# Revit family: STH21910BR_30_40_STH21910PTO_30
name_source: partatom
category: Luminárias
units: mm (PartAtom-declared; Revit-internal decimal feet)

## family parameters
Compartilhado = Não
Corte com vazios quando carregada = Não
Cota do conector redondo = Utilizar diâmetro
Fonte luminosa = Sim
Hospedeiro = Forro
Manter orientação da anotação = Não
Número OmniClass = 23.80.70.11
Ponto de cálculo do ambiente = Não
Sempre na vertical = Sim
Tipo de parte = Normal
Título OmniClass = Luminaries for Internal Lighting

## types (3) — shared parameters
Altura = 0.054 m
Comprimento = 0.075 m
Cromado = Cromado
Dimerização = Não dimerizável
Fabricante = Stella
Filtro de cor = 16777215
Grau de proteção (IP) = IP20
IRC (Índice de reprodução de cores) = >80
Largura = 0.075 m
Modelo = Easy MR11 Evo
Potência = 3 W
Tensão Elétrica = 100V-240V
Troca de temperatura da cor de lâmpada com esmaecimento = <Nenhum>
URL = https://stella.com.br
Vidro = Vidro
Ângulo de Abertura = 38°
Ângulo de inclinação = 90.00°
zero-valued in all types: Elevação padrão

## per-type parameters (varying)
| type | Arquivo de rede fotométrica | Estrutura | Fluxo Luminoso | Luminoso | Referência | Temperatura da cor (K) |
| STH21910BR/30 - BRANCO - BIVOLT - 3000K - 190lm - 38° | STELLA - STH21910BR-30 - EASY MR11 EMBUTIDO RECUADO DIRECIONÁVEL.ies | Al - Branco | 190 lm | Luminoso - 3000K | STH21910BR/30 | 3000 K |
| STH21910BR/40 - BRANCO - BIVOLT - 4000K - 200lm - 38° | STELLA - STH21910BR-40 - EASY MR11 EMBUTIDO RECUADO DIRECIONÁVEL.ies | Al - Branco | 200 lm | Luminoso - 4000K | STH21910BR/40 | 4000 K |
| STH21910PTO/30 - PRETO - BIVOLT - 3000K - 180lm - 38° | STELLA - STH21910PTO-30 - EASY MR11 EMBUTIDO RECUADO DIRECIONÁVEL.ies | Al - Preto | 180 lm | Luminoso - 3000K | STH21910PTO/30 | 3000 K |
